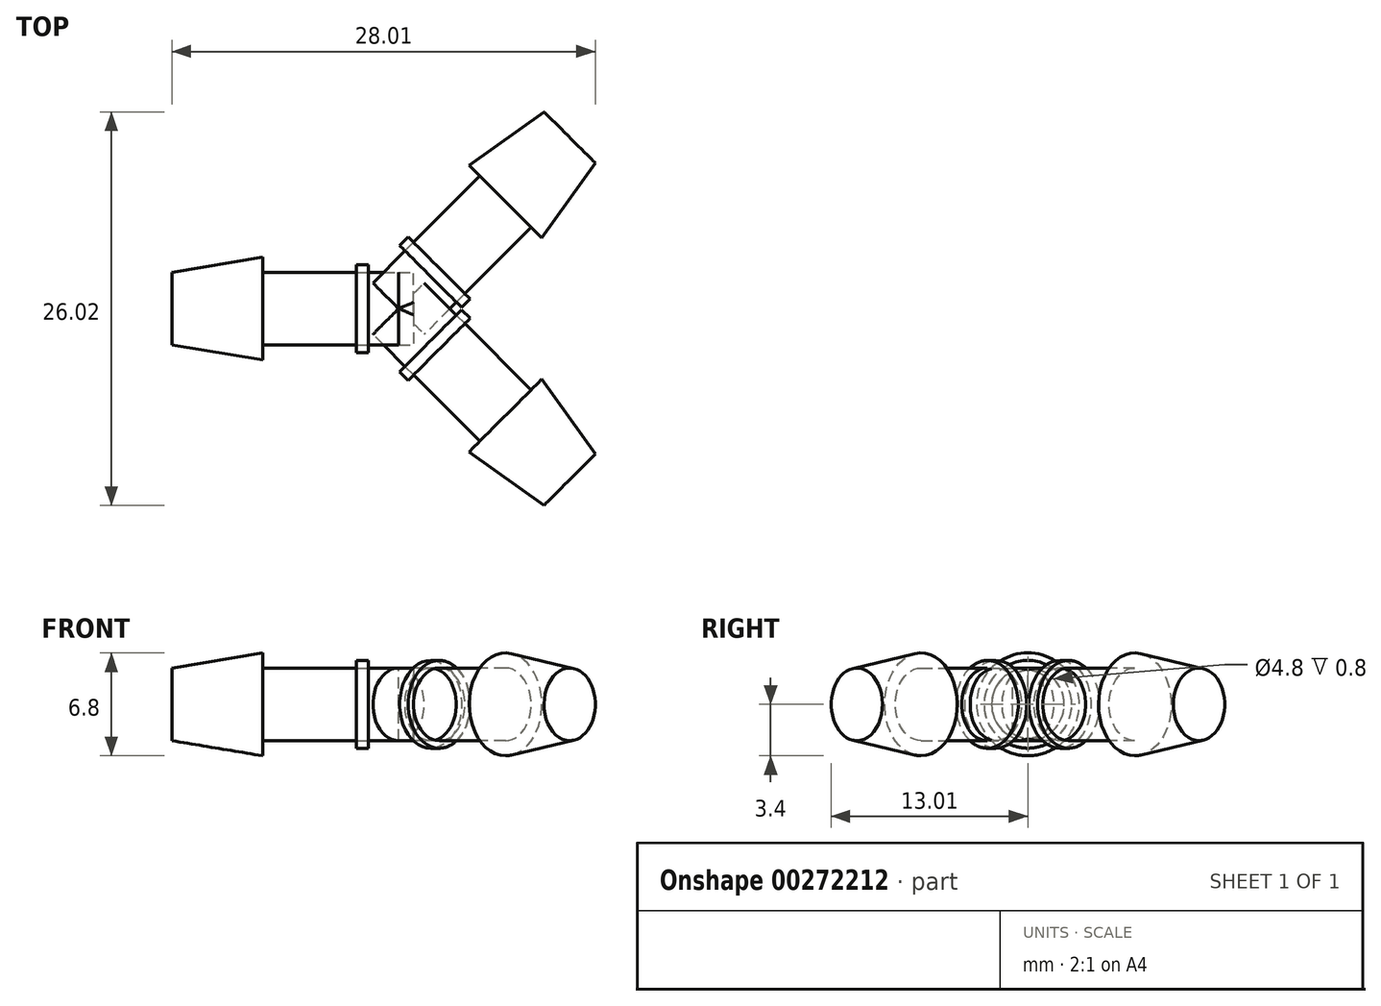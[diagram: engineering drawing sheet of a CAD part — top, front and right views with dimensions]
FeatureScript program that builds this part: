
annotation { "Feature Type Name" : "Feature", "Feature Type Description" : "" }
export const myFeature = defineFeature(function(context is Context, id is Id, definition is map)
    precondition{}
    {
        {
            var Q0;
            Q0=qCreatedBy(makeId("Front.planeOp"),FACE);
            var sketch = newSketch(context, id + "F0", { "sketchPlane" : qUnion([Q0])});
            skLineSegment(sketch, "E0.bottom", {"start": v(0, 0) * mm, "end": v(-16, 0) * mm});
            skLineSegment(sketch, "E0.top", {"start": v(0, 2.4) * mm, "end": v(-16, 2.4) * mm});
            skLineSegment(sketch, "E0.left", {"start": v(0, 0) * mm, "end": v(0, 2.4) * mm});
            skLineSegment(sketch, "E0.right", {"start": v(-16, 0) * mm, "end": v(-16, 2.4) * mm});
            skLineSegment(sketch, "E1", {"start": v(-16, 2.4) * mm, "end": v(-10, 2.4) * mm});
            skLineSegment(sketch, "E2", {"start": v(-10, 2.4) * mm, "end": v(-10, 3.4) * mm});
            skLineSegment(sketch, "E3", {"start": v(-10, 3.4) * mm, "end": v(-16, 2.4) * mm});
            skLineSegment(sketch, "E4", {"start": v(0, 2.4) * mm, "end": v(-3, 2.4) * mm});
            skLineSegment(sketch, "E5.bottom", {"start": v(-3, 2.4) * mm, "end": v(-3.8, 2.4) * mm});
            skLineSegment(sketch, "E5.top", {"start": v(-3, 2.9) * mm, "end": v(-3.8, 2.9) * mm});
            skLineSegment(sketch, "E5.left", {"start": v(-3, 2.4) * mm, "end": v(-3, 2.9) * mm});
            skLineSegment(sketch, "E5.right", {"start": v(-3.8, 2.4) * mm, "end": v(-3.8, 2.9) * mm});
            skSolve(sketch);
        }
        {
            var Q0;
            {var subQ2=sQuery(id+"F0.wireOp",EDGE,"E2");Q0=makeQuery(id+"F0.imprint","IMPRINT",FACE,{"disambiguationData":[TD([[makeQuery(id+"F0.imprint","IMPRINT",EDGE,{"derivedFrom":subQ2}),1.0]])]});}
            var Q1;
            Q1=makeQuery(id+"F0.imprint","IMPRINT",FACE,{"disambiguationData":[TD([[makeQuery(id+"F0.imprint","IMPRINT",EDGE,{"derivedFrom":sQuery(id+"F0.wireOp",EDGE,"E0.bottom")}),-1.0]])]});
            var Q2;
            Q2=sQuery(id+"F0.wireOp",EDGE,"E0.bottom");
            revolve(context, id + "F1", {"surfaceOperationType" : NewSurfaceOperationType.NEW, "entities" : qUnion([Q0, Q1]), "axis" : qUnion([Q2]), "revolveType" : RevolveType.FULL});
        }
        {
            var Q0;
            Q0=makeQuery(id+"F0.imprint","IMPRINT",FACE,{"disambiguationData":[TD([[makeQuery(id+"F0.imprint","IMPRINT",EDGE,{"derivedFrom":sQuery(id+"F0.wireOp",EDGE,"E5.top")}),1.0]])]});
            var Q1;
            Q1=sQuery(id+"F0.wireOp",EDGE,"E0.bottom");
            revolve(context, id + "F2", {"surfaceOperationType" : NewSurfaceOperationType.NEW, "entities" : qUnion([Q0]), "axis" : qUnion([Q1]), "revolveType" : RevolveType.FULL});
        }
        {
            var Q0;
            Q0=makeQuery(id+"F1.opRevolve","SWEPT_BODY",BODY,{"disambiguationData":[OSD([sQuery(id+"F0.wireOp",EDGE,"E0.bottom"),sQuery(id+"F0.wireOp",EDGE,"E0.top"),sQuery(id+"F0.wireOp",EDGE,"E0.left"),sQuery(id+"F0.wireOp",EDGE,"E0.right"),sQuery(id+"F0.wireOp",EDGE,"E2"),sQuery(id+"F0.wireOp",EDGE,"E3")])]});
            var Q1;
            Q1=makeQuery(id+"F2.opRevolve","SWEPT_BODY",BODY,{"disambiguationData":[OSD([sQuery(id+"F0.wireOp",EDGE,"E0.top"),sQuery(id+"F0.wireOp",EDGE,"E5.top"),sQuery(id+"F0.wireOp",EDGE,"E5.left"),sQuery(id+"F0.wireOp",EDGE,"E5.right")])]});
            var Q2;
            Q2=sQuery(id+"F0.wireOp",EDGE,"E0.left");
            transform(context, id + "F3", {"entities" : qUnion([Q0, Q1]), "transformType" : TransformType.ROTATION, "transformAxis" : qUnion([Q2]), "angle" : 135 * degree, "makeCopy" : true});
        }
        {
            var Q0;
            Q0=makeQuery(id+"F1.opRevolve","SWEPT_BODY",BODY,{"disambiguationData":[OSD([sQuery(id+"F0.wireOp",EDGE,"E0.bottom"),sQuery(id+"F0.wireOp",EDGE,"E0.top"),sQuery(id+"F0.wireOp",EDGE,"E0.left"),sQuery(id+"F0.wireOp",EDGE,"E0.right"),sQuery(id+"F0.wireOp",EDGE,"E2"),sQuery(id+"F0.wireOp",EDGE,"E3")])]});
            var Q1;
            Q1=makeQuery(id+"F2.opRevolve","SWEPT_BODY",BODY,{"disambiguationData":[OSD([sQuery(id+"F0.wireOp",EDGE,"E0.top"),sQuery(id+"F0.wireOp",EDGE,"E5.top"),sQuery(id+"F0.wireOp",EDGE,"E5.left"),sQuery(id+"F0.wireOp",EDGE,"E5.right")])]});
            var Q2;
            Q2=sQuery(id+"F0.wireOp",EDGE,"E0.left");
            var Q3;
            Q3=sQuery(id+"F0.wireOp",EDGE,"E0.left");
            transform(context, id + "F4", {"entities" : qUnion([Q0, Q1]), "transformType" : TransformType.ROTATION, "transformAxis" : qUnion([Q3]), "angle" : 135 * degree, "oppositeDirection" : true, "makeCopy" : true});
        }
        {
            var Q0;
            Q0=makeQuery(id+"F2.opRevolve","SWEPT_BODY",BODY,{"disambiguationData":[OSD([sQuery(id+"F0.wireOp",EDGE,"E0.top"),sQuery(id+"F0.wireOp",EDGE,"E5.top"),sQuery(id+"F0.wireOp",EDGE,"E5.left"),sQuery(id+"F0.wireOp",EDGE,"E5.right")])]});
            var Q1;
            Q1=makeQuery(id+"F1.opRevolve","SWEPT_BODY",BODY,{"disambiguationData":[OSD([sQuery(id+"F0.wireOp",EDGE,"E0.bottom"),sQuery(id+"F0.wireOp",EDGE,"E0.top"),sQuery(id+"F0.wireOp",EDGE,"E0.left"),sQuery(id+"F0.wireOp",EDGE,"E0.right"),sQuery(id+"F0.wireOp",EDGE,"E2"),sQuery(id+"F0.wireOp",EDGE,"E3")])]});
            transform(context, id + "F5", {"entities" : qUnion([Q0, Q1]), "transformType" : TransformType.TRANSLATION_3D, "dx" : 1 * mm, "dy" : 0 * mm, "dz" : 0 * mm, "makeCopy" : false});
        }
        {
            var Q0;
            Q0=makeQuery(id+"F1.opRevolve","SWEPT_FACE",FACE,{"disambiguationData":[OSD([sQuery(id+"F0.wireOp",EDGE,"E0.left")])]});
            extrude(context, id + "F6", {"entities" : qUnion([Q0]), "operationType" : NewBodyOperationType.REMOVE, "oppositeDirection" : true, "depth" : 1 * mm, "offsetDistance" : 25 * mm});
        }
    });
